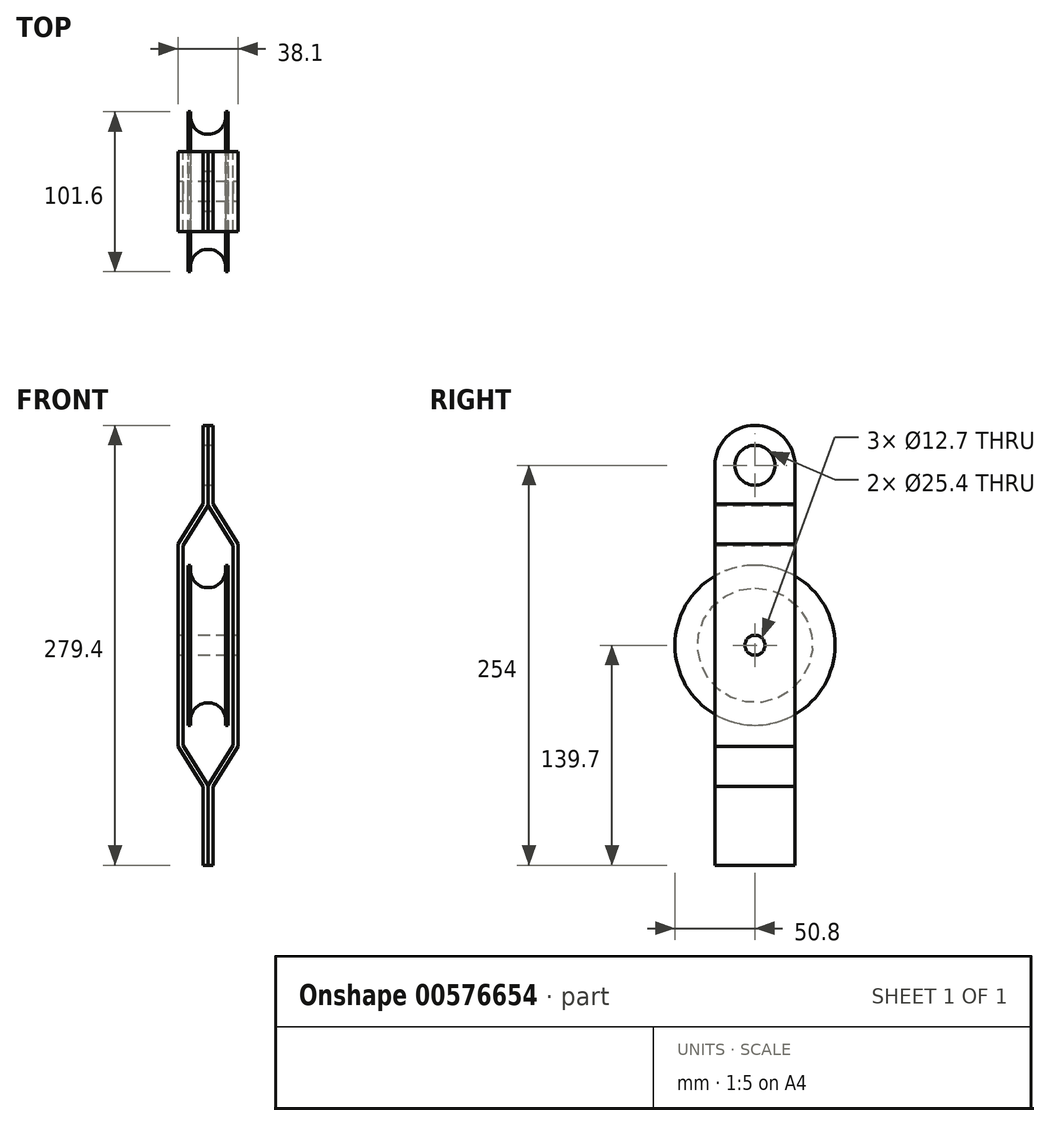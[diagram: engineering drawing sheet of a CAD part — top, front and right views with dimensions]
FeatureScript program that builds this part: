
annotation { "Feature Type Name" : "Feature", "Feature Type Description" : "" }
export const myFeature = defineFeature(function(context is Context, id is Id, definition is map)
    precondition{}
    {
        {
            var Q0;
            Q0=qCreatedBy(makeId("Front.planeOp"),FACE);
            var sketch = newSketch(context, id + "F0", { "sketchPlane" : qUnion([Q0])});
            skLineSegment(sketch, "E0.bottom", {"start": v(-12.7, 0) * mm, "end": v(12.7, 0) * mm});
            skLineSegment(sketch, "E0.top", {"start": v(-12.7, 50.8) * mm, "end": v(-11.11, 50.8) * mm});
            skLineSegment(sketch, "E0.left", {"start": v(-12.7, 0) * mm, "end": v(-12.7, 50.8) * mm});
            skLineSegment(sketch, "E0.right", {"start": v(12.7, 0) * mm, "end": v(12.7, 50.8) * mm});
            skPoint(sketch, "E0.middle", {"position": v(0, 0) * mm});
            skPoint(sketch, "E1", {"position": v(0, 47.63) * mm});
            skArc(sketch, "E2", {"start": v(-11.11, 47.63) * mm, "mid": v(0, 36.51) * mm, "end": v(11.11, 47.63) * mm});
            skLineSegment(sketch, "E3", {"start": v(-11.11, 47.63) * mm, "end": v(-11.11, 50.8) * mm});
            skLineSegment(sketch, "E4", {"start": v(11.11, 47.63) * mm, "end": v(11.11, 50.8) * mm});
            skLineSegment(sketch, "E5.trimOffspring", {"start": v(11.11, 50.8) * mm, "end": v(12.7, 50.8) * mm});
            skSolve(sketch);
        }
        {
            var Q0;
            Q0=qSketchRegion(id+"F0",true);
            var Q1;
            Q1=sQuery(id+"F0.wireOp",EDGE,"E0.bottom");
            revolve(context, id + "F1", {"entities" : qUnion([Q0]), "axis" : qUnion([Q1]), "revolveType" : RevolveType.FULL});
        }
        {
            var Q0;
            Q0=qCreatedBy(makeId("Front.planeOp"),FACE);
            var sketch = newSketch(context, id + "F2", { "sketchPlane" : qUnion([Q0])});
            skLineSegment(sketch, "E6.bottom", {"start": v(-15.88, -63.5) * mm, "end": v(15.87, -63.5) * mm, "construction": true});
            skLineSegment(sketch, "E6.top", {"start": v(-15.87, 63.5) * mm, "end": v(15.88, 63.5) * mm, "construction": true});
            skLineSegment(sketch, "E6.left", {"start": v(-15.88, -63.5) * mm, "end": v(-15.87, 63.5) * mm});
            skLineSegment(sketch, "E6.right", {"start": v(15.87, -63.5) * mm, "end": v(15.88, 63.5) * mm});
            skPoint(sketch, "E6.middle", {"position": v(0, 0) * mm});
            skLineSegment(sketch, "E7", {"start": v(-15.87, 63.5) * mm, "end": v(0, 88.9) * mm});
            skLineSegment(sketch, "E8", {"start": v(0, 88.9) * mm, "end": v(0, 139.7) * mm});
            skLineSegment(sketch, "E9.MirrorCS", {"start": v(15.88, 63.5) * mm, "end": v(0, 88.9) * mm});
            skLineSegment(sketch, "E10.MirrorCS", {"start": v(15.88, -63.5) * mm, "end": v(0, -88.9) * mm});
            skLineSegment(sketch, "E11.MirrorCS", {"start": v(-15.88, -63.5) * mm, "end": v(0, -88.9) * mm});
            skLineSegment(sketch, "E12.MirrorCS", {"start": v(0, -88.9) * mm, "end": v(0, -139.7) * mm});
            skLineSegment(sketch, "E13.0", {"start": v(-3.18, 89.81) * mm, "end": v(-3.18, 139.7) * mm});
            skLineSegment(sketch, "E13.1", {"start": v(-3.18, -89.81) * mm, "end": v(-3.17, -139.7) * mm});
            skLineSegment(sketch, "E13.2", {"start": v(-19.05, -64.41) * mm, "end": v(-3.17, -89.81) * mm});
            skLineSegment(sketch, "E13.3", {"start": v(-19.05, -64.41) * mm, "end": v(-19.05, 64.41) * mm});
            skLineSegment(sketch, "E13.4", {"start": v(-19.05, 64.41) * mm, "end": v(-3.17, 89.81) * mm});
            skLineSegment(sketch, "E14.0", {"start": v(3.18, 89.81) * mm, "end": v(3.18, 139.7) * mm});
            skLineSegment(sketch, "E14.1", {"start": v(3.17, -89.81) * mm, "end": v(3.18, -139.7) * mm});
            skLineSegment(sketch, "E14.2", {"start": v(19.05, -64.41) * mm, "end": v(3.17, -89.81) * mm});
            skLineSegment(sketch, "E14.3", {"start": v(19.05, -64.41) * mm, "end": v(19.05, 64.41) * mm});
            skLineSegment(sketch, "E14.4", {"start": v(19.05, 64.41) * mm, "end": v(3.18, 89.81) * mm});
            skLineSegment(sketch, "E15", {"start": v(-3.18, 139.7) * mm, "end": v(0, 139.7) * mm});
            skLineSegment(sketch, "E16", {"start": v(3.18, 139.7) * mm, "end": v(0, 139.7) * mm});
            skLineSegment(sketch, "E17", {"start": v(0, -139.7) * mm, "end": v(3.18, -139.7) * mm});
            skLineSegment(sketch, "E18", {"start": v(-3.17, -139.7) * mm, "end": v(0, -139.7) * mm});
            skSolve(sketch);
        }
        {
            var Q0;
            Q0=makeQuery(id+"F2.imprint","IMPRINT",FACE,{"disambiguationData":[TD([[makeQuery(id+"F2.imprint","IMPRINT",EDGE,{"derivedFrom":sQuery(id+"F2.wireOp",EDGE,"E6.right")}),-1.0]])]});
            extrude(context, id + "F3", {"entities" : qUnion([Q0]), "endBound" : BoundingType.SYMMETRIC, "depth" : 50.8 * mm, "offsetDistance" : 25.4 * mm});
        }
        {
            var Q0;
            Q0=makeQuery(id+"F2.imprint","IMPRINT",FACE,{"disambiguationData":[TD([[makeQuery(id+"F2.imprint","IMPRINT",EDGE,{"derivedFrom":sQuery(id+"F2.wireOp",EDGE,"E6.left")}),1.0]])]});
            extrude(context, id + "F4", {"entities" : qUnion([Q0]), "endBound" : BoundingType.SYMMETRIC, "depth" : 50.8 * mm, "offsetDistance" : 25.4 * mm});
        }
        {
            var Q0;
            Q0=qCreatedBy(makeId("Right.planeOp"),FACE);
            var sketch = newSketch(context, id + "F5", { "sketchPlane" : qUnion([Q0])});
            skCircle(sketch, "E19", {"center": v(0, 0) * mm, "radius": 6.35 * mm});
            skLineSegment(sketch, "E20.0", {"start": v(0, 139.7) * mm, "end": v(0, 139.7) * mm});
            skLineSegment(sketch, "E21.0", {"start": v(-25.4, 89.81) * mm, "end": v(-25.4, 114.3) * mm});
            skLineSegment(sketch, "E22.0", {"start": v(25.4, 89.81) * mm, "end": v(25.4, 114.3) * mm});
            skPoint(sketch, "E23.visualSharp", {"position": v(-25.4, 139.7) * mm});
            skArc(sketch, "E23.filletArc", {"start": v(0, 139.7) * mm, "mid": v(-17.96, 132.26) * mm, "end": v(-25.4, 114.3) * mm});
            skPoint(sketch, "E24.visualSharp", {"position": v(25.4, 139.7) * mm});
            skArc(sketch, "E24.filletArc", {"start": v(25.4, 114.3) * mm, "mid": v(17.96, 132.26) * mm, "end": v(0, 139.7) * mm});
            skArc(sketch, "E25.MirrorCS", {"start": v(25.4, -114.3) * mm, "mid": v(17.96, -132.26) * mm, "end": v(0, -139.7) * mm});
            skArc(sketch, "E26.MirrorCS", {"start": v(0, -139.7) * mm, "mid": v(-17.96, -132.26) * mm, "end": v(-25.4, -114.3) * mm});
            skLineSegment(sketch, "E27", {"start": v(0, 139.7) * mm, "end": v(-25.4, 139.7) * mm});
            skLineSegment(sketch, "E28", {"start": v(-25.4, 114.3) * mm, "end": v(-25.4, 139.7) * mm});
            skLineSegment(sketch, "E29", {"start": v(0, 139.7) * mm, "end": v(25.4, 139.7) * mm});
            skLineSegment(sketch, "E30", {"start": v(25.4, 139.7) * mm, "end": v(25.4, 114.3) * mm});
            skLineSegment(sketch, "E31.MirrorCS", {"start": v(0, -139.7) * mm, "end": v(-25.4, -139.7) * mm});
            skLineSegment(sketch, "E32.MirrorCS", {"start": v(-25.4, -114.3) * mm, "end": v(-25.4, -139.7) * mm});
            skLineSegment(sketch, "E33.MirrorCS", {"start": v(0, -139.7) * mm, "end": v(25.4, -139.7) * mm});
            skLineSegment(sketch, "E34.MirrorCS", {"start": v(25.4, -139.7) * mm, "end": v(25.4, -114.3) * mm});
            skCircle(sketch, "E35", {"center": v(0, 114.3) * mm, "radius": 12.7 * mm});
            skCircle(sketch, "E36.MirrorC", {"center": v(0, -114.3) * mm, "radius": 12.7 * mm});
            skSolve(sketch);
        }
        {
            var Q0;
            Q0=makeQuery(id+"F5.imprint","IMPRINT",FACE,{"disambiguationData":[TD([[makeQuery(id+"F5.imprint","IMPRINT",EDGE,{"derivedFrom":sQuery(id+"F5.wireOp",EDGE,"E24.filletArc")}),-1.0]])]});
            var Q1;
            Q1=makeQuery(id+"F5.imprint","IMPRINT",FACE,{"disambiguationData":[TD([[makeQuery(id+"F5.imprint","IMPRINT",EDGE,{"derivedFrom":sQuery(id+"F5.wireOp",EDGE,"E23.filletArc")}),-1.0]])]});
            var Q2;
            Q2=makeQuery(id+"F5.imprint","IMPRINT",FACE,{"disambiguationData":[TD([[makeQuery(id+"F5.imprint","IMPRINT",EDGE,{"derivedFrom":sQuery(id+"F5.wireOp",EDGE,"E25.MirrorCS")}),1.0]])]});
            var Q3;
            Q3=makeQuery(id+"F5.imprint","IMPRINT",FACE,{"disambiguationData":[TD([[makeQuery(id+"F5.imprint","IMPRINT",EDGE,{"derivedFrom":sQuery(id+"F5.wireOp",EDGE,"E26.MirrorCS")}),1.0]])]});
            var Q4;
            Q4=makeQuery(id+"F5.imprint","IMPRINT",FACE,{"disambiguationData":[TD([[makeQuery(id+"F5.imprint","IMPRINT",EDGE,{"derivedFrom":sQuery(id+"F5.wireOp",EDGE,"E19")}),1.0]])]});
            var Q5;
            Q5=makeQuery(id+"F5.imprint","IMPRINT",FACE,{"disambiguationData":[TD([[makeQuery(id+"F5.imprint","IMPRINT",EDGE,{"derivedFrom":sQuery(id+"F5.wireOp",EDGE,"E35")}),1.0]])]});
            var Q6;
            Q6=makeQuery(id+"F5.imprint","IMPRINT",FACE,{"disambiguationData":[TD([[makeQuery(id+"F5.imprint","IMPRINT",EDGE,{"derivedFrom":sQuery(id+"F5.wireOp",EDGE,"E36.MirrorC")}),-1.0]])]});
            extrude(context, id + "F6", {"entities" : qUnion([Q0, Q1, Q2, Q3, Q4, Q5, Q6]), "operationType" : NewBodyOperationType.REMOVE, "endBound" : BoundingType.SYMMETRIC, "depth" : 50.8 * mm, "offsetDistance" : 25.4 * mm});
        }
    });
